# Revit family: Shift_Classic_Easy_Chair_Offecct
name_source: partatom
category: Furniture
revit_build: Autodesk Revit 2016 (Build: 20150714_1515(x64)
units: mm (PartAtom-declared; Revit-internal decimal feet)

## family parameters
Always vertical = Yes
Cut with Voids When Loaded = No
OmniClass Number = 23.40.20.14.14.14
OmniClass Title = Settees, Sofas
Room Calculation Point = No
Shared = No
Work Plane-Based = No

## types (1)
- Shift_Classic_Easy_Chair_Offecct
    AssetType = Movable
    BIMObjectName = Shift_Classic_Easy_Chair_Offecct
    Brand = Offecct
    Category = Easy Chair
    Collection = Shift
    Color = Various
    ConvergoRefNr = 0019-1802-0001-SE
    Cost = 0 $
    Designer = Daniel Debasi and Fredrico Sandri
    DurationUnit = Year
    Finish = Legs in grey laquer, optional in silver, white or black
    HighestSeatingHeight = 380 mm
    IfcExportAs = IfcFurnishingElementType
    IfcExportType = SOFA
    LowestSeatingHeight = 380 mm
    MainColor = Various
    Manufacturer = Offecct
    ManufacturerName = Offecct
    ManufacturerURL = https://www.offecct.com
    Material = Fabric & metal
    Model = Shift Classic Easy Chair
    ModelNumber = 8151102
    Name = Shift Classic
    NominalDepth = 832 mm
    NominalHeight = 759 mm  [stored 2.49016 ft]
    NominalLength = 860 mm
    SeatingHeight = 380 mm
    Shape = Sculptured
    Size = 860x825x760 mm
    Uniclass2 = Pr_40_50_12_26
    Uniclass2015Description = Easy chairs
    Uniclass2015Reference = Pr_40_50_12_26
    Version = 1
    VersionDate = 27/08/2018
    WarrantyDurationUnit = Year

note: [stored X ft] marks values corroborated as IEEE doubles in the binary element streams (Revit-internal decimal feet)

## geometry (parser evidence)
native form markers: Sweep x5
no freeform markers — native parametric forms only
